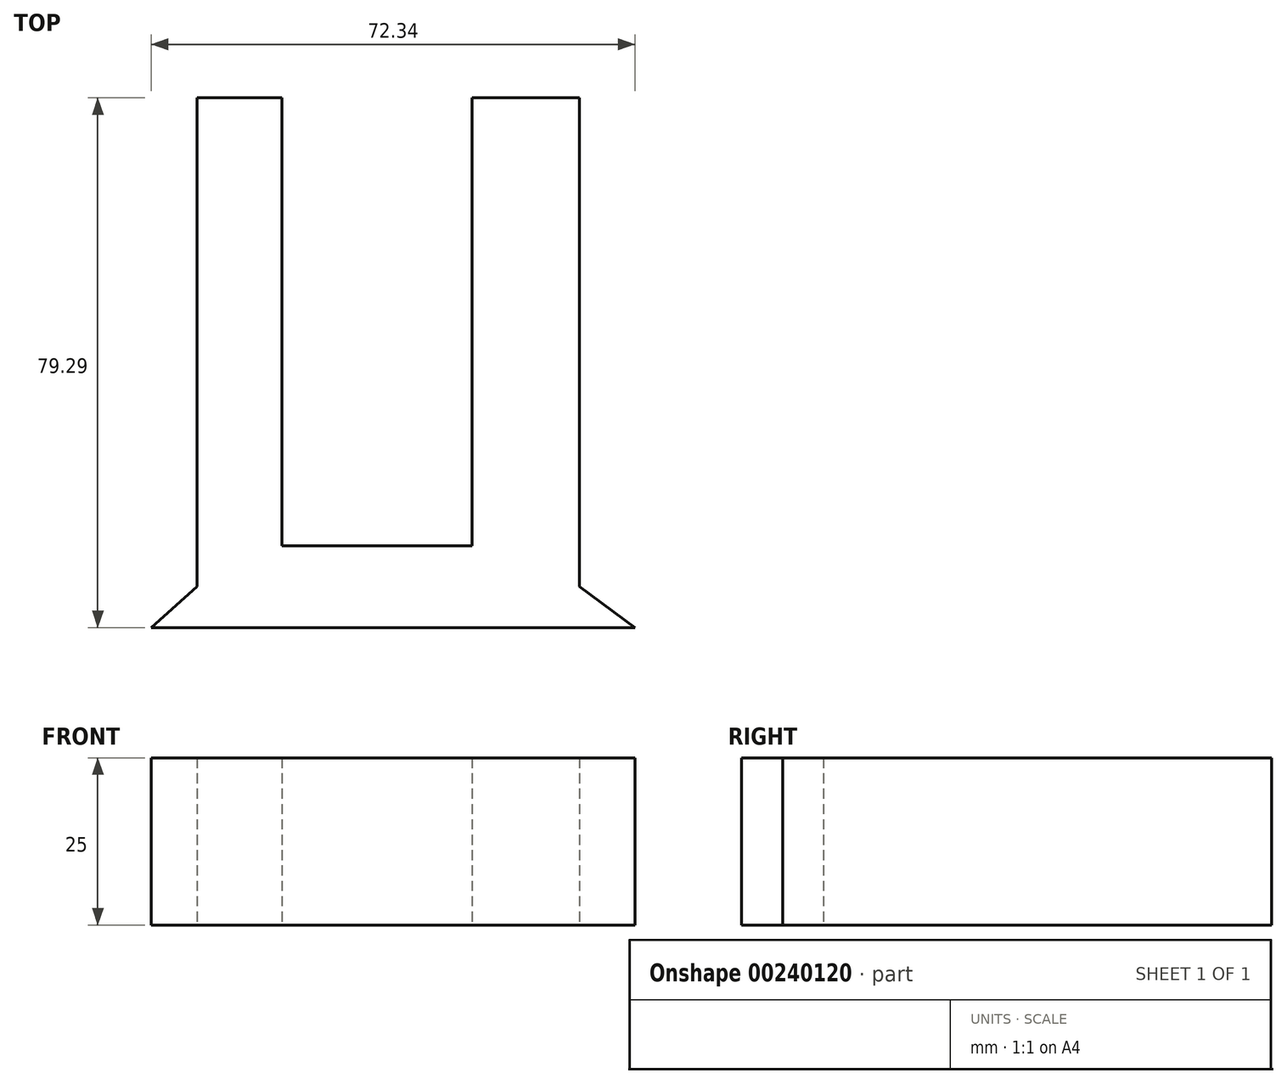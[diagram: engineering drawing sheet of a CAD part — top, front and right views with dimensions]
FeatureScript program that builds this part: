
annotation { "Feature Type Name" : "Feature", "Feature Type Description" : "" }
export const myFeature = defineFeature(function(context is Context, id is Id, definition is map)
    precondition{}
    {
        {
            var Q0;
            Q0=qCreatedBy(makeId("Top.planeOp"),FACE);
            var sketch = newSketch(context, id + "F0", { "sketchPlane" : qUnion([Q0])});
            skLineSegment(sketch, "E0", {"start": v(19.31, -16.56) * mm, "end": v(-22.7, -16.56) * mm});
            skLineSegment(sketch, "E1", {"start": v(-22.7, -16.56) * mm, "end": v(-22.7, -28.8) * mm});
            skLineSegment(sketch, "E2", {"start": v(-22.7, -28.8) * mm, "end": v(19.31, -28.8) * mm});
            skLineSegment(sketch, "E3", {"start": v(19.31, -28.8) * mm, "end": v(19.31, -16.56) * mm});
            skLineSegment(sketch, "E4", {"start": v(-22.7, -16.56) * mm, "end": v(-36.42, -28.8) * mm});
            skLineSegment(sketch, "E5", {"start": v(-36.42, -28.8) * mm, "end": v(-22.7, -28.8) * mm});
            skLineSegment(sketch, "E6", {"start": v(19.31, -16.56) * mm, "end": v(35.92, -28.8) * mm});
            skLineSegment(sketch, "E7", {"start": v(35.92, -28.8) * mm, "end": v(19.31, -28.8) * mm});
            skLineSegment(sketch, "E8", {"start": v(-29.56, -22.68) * mm, "end": v(-29.56, 50.49) * mm});
            skPoint(sketch, "E8.startSnap0", {"position": v(-22.7, -22.68) * mm});
            skLineSegment(sketch, "E9", {"start": v(-16.9, -16.56) * mm, "end": v(-16.9, 50.49) * mm});
            skLineSegment(sketch, "E10", {"start": v(11.6, -16.56) * mm, "end": v(11.6, 50.49) * mm});
            skLineSegment(sketch, "E11", {"start": v(11.6, 50.49) * mm, "end": v(27.62, 50.49) * mm});
            skLineSegment(sketch, "E12", {"start": v(27.62, 50.49) * mm, "end": v(27.62, -22.68) * mm});
            skLineSegment(sketch, "E13", {"start": v(-29.56, 50.49) * mm, "end": v(-16.9, 50.49) * mm});
            skLineSegment(sketch, "E14", {"start": v(-16.9, 50.49) * mm, "end": v(11.6, 50.49) * mm, "construction": true});
            skLineSegment(sketch, "E15", {"start": v(-29.56, -22.68) * mm, "end": v(27.62, -22.68) * mm, "construction": true});
            skSolve(sketch);
        }
        {
            var Q0;
            {var subQ4=sQuery(id+"F0.wireOp",EDGE,"E8");Q0=makeQuery(id+"F0.imprint","IMPRINT",FACE,{"disambiguationData":[TD([[makeQuery(id+"F0.imprint","IMPRINT",EDGE,{"derivedFrom":subQ4}),-1.0]])]});}
            var Q1;
            {var subQ0=sQuery(id+"F0.wireOp",EDGE,"E10");Q1=makeQuery(id+"F0.imprint","IMPRINT",FACE,{"disambiguationData":[TD([[makeQuery(id+"F0.imprint","IMPRINT",EDGE,{"derivedFrom":subQ0}),-1.0]])]});}
            var Q2;
            {var subQ0=sQuery(id+"F0.wireOp",EDGE,"E1");Q2=makeQuery(id+"F0.imprint","IMPRINT",FACE,{"disambiguationData":[TD([[makeQuery(id+"F0.imprint","IMPRINT",EDGE,{"derivedFrom":subQ0}),1.0]])]});}
            var Q3;
            {var subQ0=sQuery(id+"F0.wireOp",EDGE,"E1");Q3=makeQuery(id+"F0.imprint","IMPRINT",FACE,{"disambiguationData":[TD([[makeQuery(id+"F0.imprint","IMPRINT",EDGE,{"derivedFrom":subQ0}),-1.0]])]});}
            var Q4;
            {var subQ0=sQuery(id+"F0.wireOp",EDGE,"E3");Q4=makeQuery(id+"F0.imprint","IMPRINT",FACE,{"disambiguationData":[TD([[makeQuery(id+"F0.imprint","IMPRINT",EDGE,{"derivedFrom":subQ0}),-1.0]])]});}
            extrude(context, id + "F1", {"entities" : qUnion([Q0, Q1, Q2, Q3, Q4]), "depth" : 25 * mm});
        }
    });
